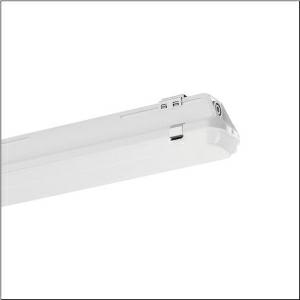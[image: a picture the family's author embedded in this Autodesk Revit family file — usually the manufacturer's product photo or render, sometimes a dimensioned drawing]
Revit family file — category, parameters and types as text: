
# Revit family: monsun_21_51fb10dp660c
name_source: partatom
category: Lighting Fixtures
units: mm (PartAtom-declared; Revit-internal decimal feet)

## family parameters
Cut with Voids When Loaded = No
Host = Face
Light Source = No
Part Type = Normal
Room Calculation Point = No
Round Connector Dimension = Use Diameter
Shared = No

## types (1)
- --- (1 x LED, 6060 lm, 33.7 W, 6500K)
    Apparent Load = 34 VA
    CIE Flux Codes = 47 77 93 94 100
    Color Rendering = 80
    Color Temperature = 6500K
    Default Elevation = 1800 mm
    Description = Monsun 21, damp-proof luminaire, chain hanger, primary optical cover: enclosure, of PMMA, light emission: direct distribution, primary light characteristic: symmetric, installation type: suspended mounting, surface-mounted, horizontal mounting, vertical mounting, LED, rated luminous flux: 6.060lm, luminous efficacy: 180lm/W, light colour: 865, colour temperature: 6500K, control gear: DALI 2, with terminal, 5-pole, max. 2.5mm², mains connection: 220..240V, AC, 50/60Hz, rated input power: 34W, housing, of glass-fibre reinforced polyester, uncoated, bright grey, incl. chain hanger, length: 1.590mm, width: 90mm, height: 88mm, clip for enclosure, of stainless steel (V2A), ceiling mounting element, of stainless steel (V2A), chain hanger, of stainless steel (V2A), protection rating (complete): IP66, insulation class (complete): insulation class I (protective earthing), certification: CE, ENEC, VDE, UKCA, protection symbol: D, impact resistance: IK04, permissible operating ambient temperature: -25..+35°C, standard: EN 50419, EN 60598-2-1, corresponds to IFS (International Featured Standards) requirements for safety and quality in the food industry, for indoor or canopied outdoor use, no direct snow, no direct sun, no direct rain, LABS conformity tested according to VDMA 24364:2018-05, contact your sales advisor before using the luminaires in applications with unclear chemical exposure, large temperature fluctuations or condensation-forming humidity, packaging unit: 1 piece
    Height = 89 mm
    Lamp = 1 x LED
    Lamp Light Flux = 6060 lm
    Lamp Power = 33.7 W
    Lamp count = 1
    Length = 1590 mm
    Luminous efficacy = 180 lm/W
    Manufacturer = Siteco
    ModVariant = No
    Model = 51FB10DP660C
    Mounting Place = Ceiling
    Mounting Type = Surface mounted
    Number of Poles = 1
    OnlyDefault = Yes
    Power Factor = 1
    Product Name = Monsun 21
    Product group = damp-proof luminaire
    ProductGroupID = 300
    Protection Class = Protection class I
    Protection Degree = IP 66
    RLX_Detail_Level = 1
    RLX_Emergency_Light_Flux = 0 lm
    RLX_Emergency_Type = 0
    RLX_Emergency_Type_DB = No
    RlxData = <blob elided: 92221 chars, md5=ac0f736e>
    Socket = socket
    Standby Power = 0 W
    System Light Flux = 6060 lm
    System Power = 34 W
    Type Comments = factory setting: luminous flux: 100 % | dim-lin: 254 | 237 mA
    Type Image = l_1319656.jpg
    URL = http://relux.com
    VarID = @adj_038693
    Voltage = 0 V
    Weight = 0.00 kg
    Width = 90 mm

## geometry (parser evidence)
native form markers: Blend x4, Sweep x14
no freeform markers — native parametric forms only
